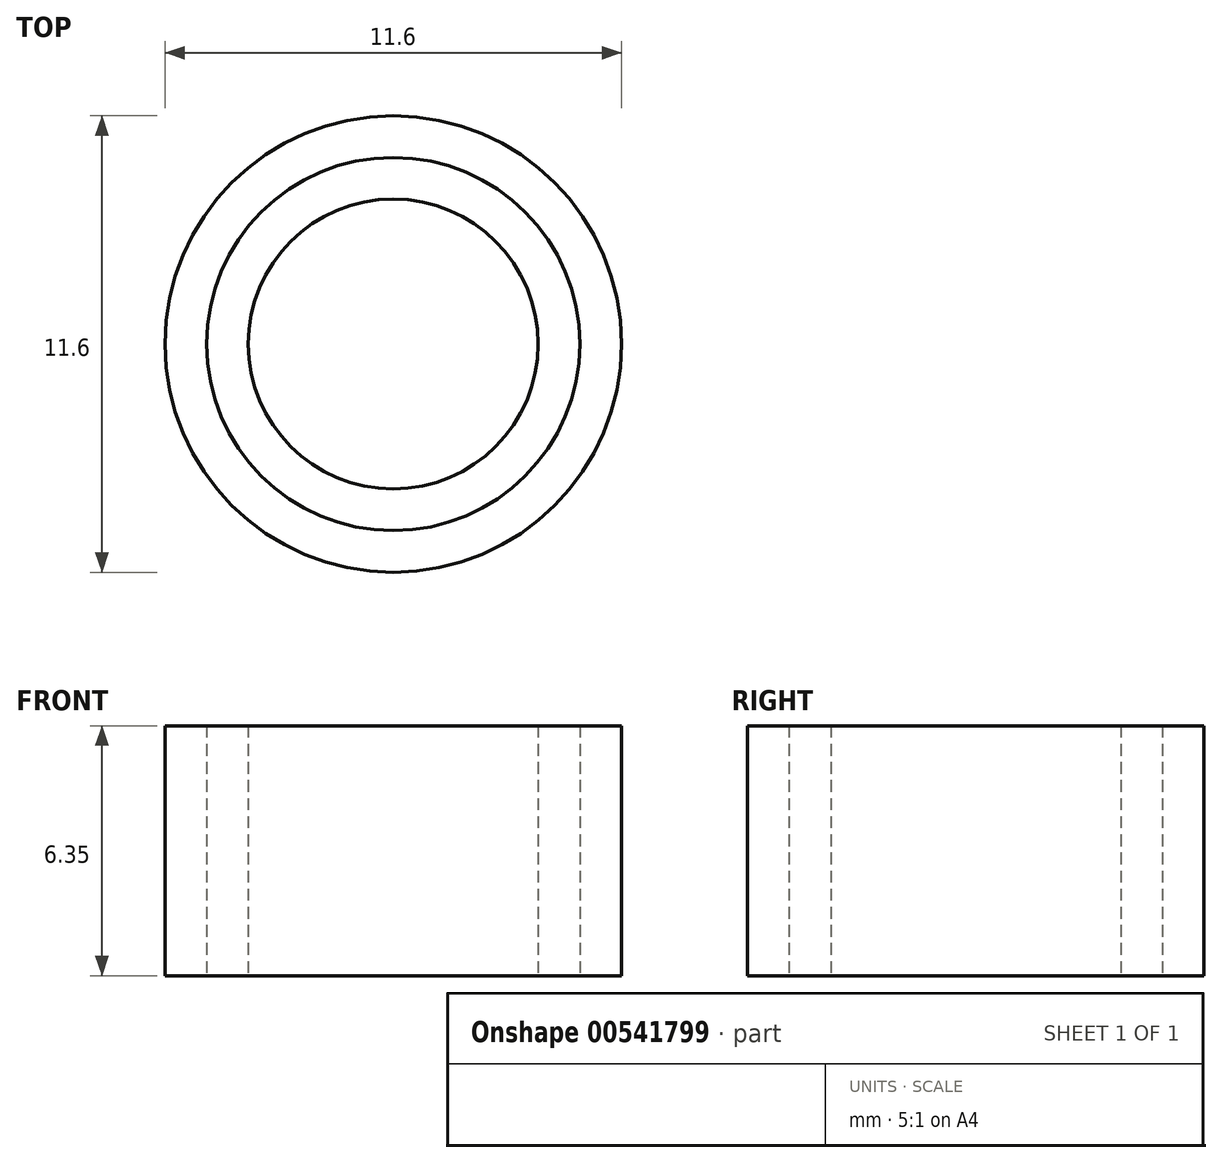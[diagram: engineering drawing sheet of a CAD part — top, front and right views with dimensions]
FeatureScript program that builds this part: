
annotation { "Feature Type Name" : "Feature", "Feature Type Description" : "" }
export const myFeature = defineFeature(function(context is Context, id is Id, definition is map)
    precondition{}
    {
        {
            var Q0;
            Q0=qCreatedBy(makeId("Top.planeOp"),FACE);
            var sketch = newSketch(context, id + "F0", { "sketchPlane" : qUnion([Q0])});
            skCircle(sketch, "E0", {"center": v(0, 0) * mm, "radius": 6.35 * mm, "construction": true});
            skCircle(sketch, "E1", {"center": v(0, 0) * mm, "radius": 3.68 * mm});
            skSolve(sketch);
        }
        {
            var Q0;
            Q0 = qSketchRegion(id + "F0", true);
            extrude(context, id + "F1", {"entities" : qUnion([Q0]), "depth" : 6.35 * mm, "offsetDistance" : 25.4 * mm});
        }
        {
            var Q0;
            Q0=qCreatedBy(makeId("Top.planeOp"),FACE);
            var sketch = newSketch(context, id + "F2", { "sketchPlane" : qUnion([Q0])});
            skCircle(sketch, "E2", {"center": v(0, 0) * mm, "radius": 7.4 * mm, "construction": true});
            skCircle(sketch, "E3", {"center": v(0, 0) * mm, "radius": 4.74 * mm});
            skSolve(sketch);
        }
        {
            var Q0;
            Q0 = qSketchRegion(id + "F2", true);
            extrude(context, id + "F3", {"entities" : qUnion([Q0]), "depth" : 6.35 * mm, "offsetDistance" : 25.4 * mm});
        }
        {
            var Q0;
            Q0=qCreatedBy(makeId("Top.planeOp"),FACE);
            var sketch = newSketch(context, id + "F4", { "sketchPlane" : qUnion([Q0])});
            skCircle(sketch, "E4", {"center": v(0, 0) * mm, "radius": 8.47 * mm, "construction": true});
            skCircle(sketch, "E5", {"center": v(0, 0) * mm, "radius": 5.8 * mm});
            skSolve(sketch);
        }
        {
            var Q0;
            Q0 = qSketchRegion(id + "F4", true);
            extrude(context, id + "F5", {"entities" : qUnion([Q0]), "depth" : 6.35 * mm, "offsetDistance" : 25.4 * mm});
        }
    });
